# Revit family: Andy v5.5
name_source: partatom
category: Entourage
units: mm (PartAtom-declared; Revit-internal decimal feet)

## family parameters
Always vertical = Yes
Cut with Voids When Loaded = No
Render Appearance Source = Family Geometry
Room Calculation Point = No
Shared = No
Work Plane-Based = No

## types (10) — shared parameters
Description = Multi-positionable human with multiple body profiles for use in 3D views and rendering
Hip Azimuth = 0.00°
Hip Azimuth Label = 1.00°
Inspecting = No
Kinship = www.kinship.io
Kneeling = No
Left Ankle Azimuth Label = 1.00°
Left Thigh Azimuth Label = 1.00°
Length 1 = 0.167 '
Manufacturer = Kinship
Min Angle = 1.00°
Model = Andy v5.5
Neck Rotation = 90.00°
Neck Rotation Label = 90.00°
Praying = No
Right Ankle Azimuth Label = 1.00°
Right Ankle Pitch Label = 181.00°
Right Hand Azimuth = 90.00°
Right Hand Azimuth Label = 90.00°
Right Thigh Azimuth Label = 1.00°
Running = No
Sitting = No
Standing = Yes
Torso Pitch = 91.00°
URL = www.kinship.io
Walking = No
zero-valued in all types: Height

## per-type parameters (varying)
- Walking 1 - Child 2: Ankle Radius=0.071 '; Ankle Radius 2=0.071 '; Calf Length=0.882 '; Chest Depth=0.682 '; Chest Half Depth=0.341 '; Chest Half Depth Back Label=0.288 '; Chest Half Depth Front Label=0.395 '; Chest Half Width=0.427 '; Chest Offset=0.054 '; Chest Width=0.853 '; Chest to Shoulder Height=0.252 '; Child=Yes; Chin to Eye Height=0.338 '; Elbow Radius=0.064 '; Elbow Radius 2=0.064 '; Female=Yes; Foot Height=0.212 '; Foot Length=0.547 '; Foot Width Radius=0.114 '; Fore Arm Length=0.679 '; Hand Depth=0.079 '; Hand Half Depth=0.039 '; Hand Half Length=0.194 '; Hand Half Width=0.102 '; Hand Length=0.388 '; Hand Width=0.204 '; Head Azimuth=0.00°; Head Azimuth Label=1.00°; Head Back Depth=0.199 '; Head Depth=0.569 '; Head Front Depth=0.37 '; Head Half Height=0.355 '; Head Half Width=0.22 '; Head Height=0.711 '; Head Pitch=90.00°; Head Width=0.439 '; Heel Radius=0.071 '; Hip Depth=0.463 '; Hip Half Depth=0.231 '; Hip Half Width=0.38 '; Hip Height=2.187 '; Hip Width=0.759 '; Hip to Waist Height=0.355 '; Knee Radius=0.114 '; Knee Radius 2=0.114 '; Left Ankle Azimuth=0.00°; Left Ankle Pitch=184.00°; Left Ankle Pitch Label=184.00°; Left Arm Azimuth=-20.00°; Left Arm Azimuth Label=-20.00°; Left Arm Pitch=-60.00°; Left Arm Pitch Label=-60.00°; Left Elbow Azimuth=230.00°; Left Elbow Azimuth Label=230.00°; Left Hand Azimuth=90.00°; Left Hand Azimuth Label=90.00°; Left Hand Pitch=40.00°; Left Hand Pitch Label=40.00°; Left Hand Rotation=170.00°; Left Hand Rotation Label=170.00°; Left Knee Pitch=173.00°; Left Knee Pitch Label=173.00°; Left Thigh Azimuth=1.00°; Left Thigh Pitch=105.00°; Left Thigh Pitch Label=105.00°; Length 10=-0.039 '; Length 11=0.026 '; Length 2=0.362 '; Length 3=-0.212 '; Length 4=-0.212 '; Length 5=-0.711 '; Length 6=-0.252 '; Length 7=0.199 '; Length 8=0.15 '; Length 9=0.136 '; Male 1=Yes; Male 2=No; Neck Height=0.213 '; Neck Pitch=90.00°; Neck Pitch Label=90.00°; Neck Radius=0.111 '; Right Ankle Azimuth=0.00°; Right Ankle Pitch=181.00°; Right Arm Azimuth=10.00°; Right Arm Azimuth Label=10.00°; Right Arm Pitch=105.00°; Right Arm Pitch Label=105.00°; Right Elbow Azimuth=135.00°; Right Elbow Azimuth Label=135.00°; Right Hand Pitch=10.00°; Right Hand Pitch Label=10.00°; Right Hand Rotation=10.00°; Right Hand Rotation Label=10.00°; Right Knee Pitch=123.00°; Right Knee Pitch Label=123.00°; Right Thigh Azimuth=1.00°; Right Thigh Pitch=94.00°; Right Thigh Pitch Label=94.00°; Shoulder Depth=0.422 '; Shoulder Half Depth=0.211 '; Shoulder Half Width 1=0.414 '; Shoulder Half Width 2=0.517 '; Shoulder Radius=0.103 '; Shoulder Radius 2=0.103 '; Shoulder Width=1.034 '; Shoulder to Neck Base Height=0.245 '; Thigh Length=1.094 '; Thigh Radius=0.185 '; Thigh Radius 2=0.185 '; Torso Azimuth=92.00°; Total Height=4.265 '; Type Comments=Walking position 4.25 ft child.; Upper Arm Length=0.782 '; Upper Arm Radius=0.126 '; Waist Depth=0.509 '; Waist Half Depth=0.255 '; Waist Half Depth Back Label=0.255 '; Waist Half Depth Front Label=0.255 '; Waist Half Width=0.345 '; Waist Offset=0 '; Waist Width=0.69 '; Waist to Chest Height=0.711 '; Wrist Radius=0.039 '; Wrist Radius 2=0.039 '; a=1.056 '; b=1.083 '; c=0.091 '
- Walking 2 - Female: Ankle Radius=0.088 '; Ankle Radius 2=0.088 '; Calf Length=1.102 '; Chest Depth=0.853 '; Chest Half Depth=0.427 '; Chest Half Depth Back Label=0.3 '; Chest Half Depth Front Label=0.553 '; Chest Half Width=0.533 '; Chest Offset=0.126 '; Chest Width=1.066 '; Chest to Shoulder Height=0.316 '; Child=No; Chin to Eye Height=0.344 '; Elbow Radius=0.08 '; Elbow Radius 2=0.08 '; Female=Yes; Foot Height=0.265 '; Foot Length=0.684 '; Foot Width Radius=0.143 '; Fore Arm Length=0.848 '; Hand Depth=0.091 '; Hand Half Depth=0.045 '; Hand Half Length=0.242 '; Hand Half Width=0.128 '; Hand Length=0.485 '; Hand Width=0.255 '; Head Azimuth=0.00°; Head Azimuth Label=1.00°; Head Back Depth=0.193 '; Head Depth=0.55 '; Head Front Depth=0.358 '; Head Half Height=0.344 '; Head Half Width=0.213 '; Head Height=0.688 '; Head Pitch=90.00°; Head Width=0.425 '; Heel Radius=0.088 '; Hip Depth=0.579 '; Hip Half Depth=0.289 '; Hip Half Width=0.474 '; Hip Height=2.734 '; Hip Width=0.949 '; Hip to Waist Height=0.344 '; Knee Radius=0.143 '; Knee Radius 2=0.143 '; Left Ankle Azimuth=0.00°; Left Ankle Pitch=184.00°; Left Ankle Pitch Label=184.00°; Left Arm Azimuth=10.00°; Left Arm Azimuth Label=10.00°; Left Arm Pitch=-60.00°; Left Arm Pitch Label=-60.00°; Left Elbow Azimuth=230.00°; Left Elbow Azimuth Label=230.00°; Left Hand Azimuth=90.00°; Left Hand Azimuth Label=90.00°; Left Hand Pitch=5.00°; Left Hand Pitch Label=5.00°; Left Hand Rotation=-90.00°; Left Hand Rotation Label=-90.00°; Left Knee Pitch=173.00°; Left Knee Pitch Label=173.00°; Left Thigh Azimuth=1.00°; Left Thigh Pitch=105.00°; Left Thigh Pitch Label=105.00°; Length 10=-0.045 '; Length 11=0.03 '; Length 2=0.452 '; Length 3=-0.265 '; Length 4=-0.265 '; Length 5=-0.989 '; Length 6=-0.316 '; Length 7=0.193 '; Length 8=0.145 '; Length 9=0.131 '; Male 1=Yes; Male 2=No; Neck Height=0.407 '; Neck Pitch=90.00°; Neck Pitch Label=90.00°; Neck Radius=0.139 '; Right Ankle Azimuth=0.00°; Right Ankle Pitch=181.00°; Right Arm Azimuth=10.00°; Right Arm Azimuth Label=10.00°; Right Arm Pitch=105.00°; Right Arm Pitch Label=105.00°; Right Elbow Azimuth=135.00°; Right Elbow Azimuth Label=135.00°; Right Hand Pitch=10.00°; Right Hand Pitch Label=10.00°; Right Hand Rotation=10.00°; Right Hand Rotation Label=10.00°; Right Knee Pitch=123.00°; Right Knee Pitch Label=123.00°; Right Thigh Azimuth=1.00°; Right Thigh Pitch=94.00°; Right Thigh Pitch Label=94.00°; Shoulder Depth=0.527 '; Shoulder Half Depth=0.264 '; Shoulder Half Width 1=0.517 '; Shoulder Half Width 2=0.646 '; Shoulder Radius=0.129 '; Shoulder Radius 2=0.129 '; Shoulder Width=1.292 '; Shoulder to Neck Base Height=0.266 '; Thigh Length=1.367 '; Thigh Radius=0.231 '; Thigh Radius 2=0.231 '; Torso Azimuth=92.00°; Total Height=5.331 '; Type Comments=Walking position 5.3 ft female.; Upper Arm Length=0.977 '; Upper Arm Radius=0.157 '; Waist Depth=0.445 '; Waist Half Depth=0.223 '; Waist Half Depth Back Label=0.223 '; Waist Half Depth Front Label=0.223 '; Waist Half Width=0.365 '; Waist Offset=0 '; Waist Width=0.73 '; Waist to Chest Height=0.989 '; Wrist Radius=0.045 '; Wrist Radius 2=0.045 '; a=1.32 '; b=1.354 '; c=0.114 '
- Walking 4 - Male 2: Ankle Radius=0.125 '; Ankle Radius 2=0.125 '; Calf Length=1.191 '; Chest Depth=0.738 '; Chest Half Depth=0.369 '; Chest Half Depth Back Label=0.369 '; Chest Half Depth Front Label=0.369 '; Chest Half Width=0.591 '; Chest Offset=0 '; Chest Width=1.181 '; Chest to Shoulder Height=0.309 '; Child=No; Chin to Eye Height=0.394 '; Elbow Radius=0.113 '; Elbow Radius 2=0.113 '; Female=No; Foot Height=0.286 '; Foot Length=0.844 '; Foot Width Radius=0.203 '; Fore Arm Length=0.94 '; Hand Depth=0.161 '; Hand Half Depth=0.081 '; Hand Half Length=0.268 '; Hand Half Width=0.166 '; Hand Length=0.537 '; Hand Width=0.332 '; Head Azimuth=0.00°; Head Azimuth Label=1.00°; Head Back Depth=0.22 '; Head Depth=0.63 '; Head Front Depth=0.409 '; Head Half Height=0.394 '; Head Half Width=0.262 '; Head Height=0.787 '; Head Pitch=90.00°; Head Width=0.525 '; Heel Radius=0.125 '; Hip Depth=0.821 '; Hip Half Depth=0.41 '; Hip Half Width=0.607 '; Hip Height=2.953 '; Hip Width=1.215 '; Hip to Waist Height=0.394 '; Knee Radius=0.203 '; Knee Radius 2=0.203 '; Left Ankle Azimuth=0.00°; Left Ankle Pitch=184.00°; Left Ankle Pitch Label=184.00°; Left Arm Azimuth=10.00°; Left Arm Azimuth Label=10.00°; Left Arm Pitch=-105.00°; Left Arm Pitch Label=-105.00°; Left Elbow Azimuth=182.00°; Left Elbow Azimuth Label=182.00°; Left Hand Azimuth=90.00°; Left Hand Azimuth Label=90.00°; Left Hand Pitch=5.00°; Left Hand Pitch Label=5.00°; Left Hand Rotation=-90.00°; Left Hand Rotation Label=-90.00°; Left Knee Pitch=173.00°; Left Knee Pitch Label=173.00°; Left Thigh Azimuth=1.00°; Left Thigh Pitch=105.00°; Left Thigh Pitch Label=105.00°; Length 10=-0.081 '; Length 11=0.054 '; Length 2=0.515 '; Length 3=-0.286 '; Length 4=-0.286 '; Length 5=-1.083 '; Length 6=-0.309 '; Length 7=0.22 '; Length 8=0.147 '; Length 9=0.131 '; Male 1=No; Male 2=Yes; Neck Height=0.433 '; Neck Pitch=90.00°; Neck Pitch Label=90.00°; Neck Radius=0.182 '; Right Ankle Azimuth=0.00°; Right Ankle Pitch=181.00°; Right Arm Azimuth=10.00°; Right Arm Azimuth Label=10.00°; Right Arm Pitch=90.00°; Right Arm Pitch Label=90.00°; Right Elbow Azimuth=145.00°; Right Elbow Azimuth Label=145.00°; Right Hand Pitch=10.00°; Right Hand Pitch Label=10.00°; Right Hand Rotation=10.00°; Right Hand Rotation Label=10.00°; Right Knee Pitch=123.00°; Right Knee Pitch Label=123.00°; Right Thigh Azimuth=1.00°; Right Thigh Pitch=94.00°; Right Thigh Pitch Label=94.00°; Shoulder Depth=0.591 '; Shoulder Half Depth=0.295 '; Shoulder Half Width 1=0.556 '; Shoulder Half Width 2=0.738 '; Shoulder Radius=0.183 '; Shoulder Radius 2=0.183 '; Shoulder Width=1.476 '; Shoulder to Neck Base Height=0.34 '; Thigh Length=1.476 '; Thigh Radius=0.328 '; Thigh Radius 2=0.328 '; Torso Azimuth=92.00°; Total Height=5.906 '; Type Comments=Walking position 6 ft male 2.; Upper Arm Length=1.083 '; Upper Arm Radius=0.223 '; Waist Depth=1.067 '; Waist Half Depth=0.534 '; Waist Half Depth Back Label=0.399 '; Waist Half Depth Front Label=0.669 '; Waist Half Width=0.607 '; Waist Offset=0.135 '; Waist Width=1.215 '; Waist to Chest Height=1.083 '; Wrist Radius=0.081 '; Wrist Radius 2=0.081 '; a=1.426 '; b=1.462 '; c=0.137 '
- Walking 3 - Male 1: Ankle Radius=0.109 '; Ankle Radius 2=0.109 '; Calf Length=1.124 '; Chest Depth=0.744 '; Chest Half Depth=0.372 '; Chest Half Depth Back Label=0.327 '; Chest Half Depth Front Label=0.416 '; Chest Half Width=0.558 '; Chest Offset=0.045 '; Chest Width=1.115 '; Chest to Shoulder Height=0.306 '; Child=No; Chin to Eye Height=0.372 '; Elbow Radius=0.098 '; Elbow Radius 2=0.098 '; Female=No; Foot Height=0.27 '; Foot Length=0.797 '; Foot Width Radius=0.177 '; Fore Arm Length=0.887 '; Hand Depth=0.14 '; Hand Half Depth=0.07 '; Hand Half Length=0.254 '; Hand Half Width=0.157 '; Hand Length=0.507 '; Hand Width=0.313 '; Head Azimuth=0.00°; Head Azimuth Label=1.00°; Head Back Depth=0.208 '; Head Depth=0.595 '; Head Front Depth=0.387 '; Head Half Height=0.372 '; Head Half Width=0.248 '; Head Height=0.744 '; Head Pitch=90.00°; Head Width=0.496 '; Heel Radius=0.109 '; Hip Depth=0.715 '; Hip Half Depth=0.358 '; Hip Half Width=0.558 '; Hip Height=2.789 '; Hip Width=1.115 '; Hip to Waist Height=0.372 '; Knee Radius=0.177 '; Knee Radius 2=0.177 '; Left Ankle Azimuth=0.00°; Left Ankle Pitch=184.00°; Left Ankle Pitch Label=184.00°; Left Arm Azimuth=182.00°; Left Arm Azimuth Label=182.00°; Left Arm Pitch=-90.00°; Left Arm Pitch Label=-90.00°; Left Elbow Azimuth=145.00°; Left Elbow Azimuth Label=145.00°; Left Hand Azimuth=90.00°; Left Hand Azimuth Label=90.00°; Left Hand Pitch=5.00°; Left Hand Pitch Label=5.00°; Left Hand Rotation=60.00°; Left Hand Rotation Label=60.00°; Left Knee Pitch=173.00°; Left Knee Pitch Label=173.00°; Left Thigh Azimuth=1.00°; Left Thigh Pitch=105.00°; Left Thigh Pitch Label=105.00°; Length 10=-0.07 '; Length 11=0.047 '; Length 2=0.511 '; Length 3=-0.27 '; Length 4=-0.27 '; Length 5=-1.023 '; Length 6=-0.306 '; Length 7=0.208 '; Length 8=0.139 '; Length 9=0.124 '; Male 1=Yes; Male 2=No; Neck Height=0.409 '; Neck Pitch=90.00°; Neck Pitch Label=90.00°; Neck Radius=0.142 '; Right Ankle Azimuth=0.00°; Right Ankle Pitch=181.00°; Right Arm Azimuth=10.00°; Right Arm Azimuth Label=10.00°; Right Arm Pitch=105.00°; Right Arm Pitch Label=105.00°; Right Elbow Azimuth=160.00°; Right Elbow Azimuth Label=160.00°; Right Hand Pitch=10.00°; Right Hand Pitch Label=10.00°; Right Hand Rotation=90.00°; Right Hand Rotation Label=90.00°; Right Knee Pitch=123.00°; Right Knee Pitch Label=123.00°; Right Thigh Azimuth=1.00°; Right Thigh Pitch=94.00°; Right Thigh Pitch Label=94.00°; Shoulder Depth=0.46 '; Shoulder Half Depth=0.23 '; Shoulder Half Width 1=0.538 '; Shoulder Half Width 2=0.697 '; Shoulder Radius=0.159 '; Shoulder Radius 2=0.159 '; Shoulder Width=1.394 '; Shoulder to Neck Base Height=0.308 '; Thigh Length=1.394 '; Thigh Radius=0.286 '; Thigh Radius 2=0.286 '; Torso Azimuth=92.00°; Total Height=5.577 '; Type Comments=Walking position 5.5 ft male 1.; Upper Arm Length=1.023 '; Upper Arm Radius=0.194 '; Waist Depth=0.65 '; Waist Half Depth=0.325 '; Waist Half Depth Back Label=0.3 '; Waist Half Depth Front Label=0.35 '; Waist Half Width=0.507 '; Waist Offset=0.025 '; Waist Width=1.014 '; Waist to Chest Height=1.023 '; Wrist Radius=0.07 '; Wrist Radius 2=0.07 '; a=1.347 '; b=1.381 '; c=0.131 '
- Standing 2 - Child 2: Ankle Radius=0.09 '; Ankle Radius 2=0.09 '; Calf Length=0.959 '; Chest Depth=0.634 '; Chest Half Depth=0.317 '; Chest Half Depth Back Label=0.309 '; Chest Half Depth Front Label=0.326 '; Chest Half Width=0.476 '; Chest Offset=0.008 '; Chest Width=0.951 '; Chest to Shoulder Height=0.265 '; Child=Yes; Chin to Eye Height=0.378 '; Elbow Radius=0.081 '; Elbow Radius 2=0.081 '; Female=No; Foot Height=0.23 '; Foot Length=0.68 '; Foot Width Radius=0.146 '; Fore Arm Length=0.757 '; Hand Depth=0.1 '; Hand Half Depth=0.05 '; Hand Half Length=0.216 '; Hand Half Width=0.134 '; Hand Length=0.432 '; Hand Width=0.267 '; Head Azimuth=30.00°; Head Azimuth Label=30.00°; Head Back Depth=0.222 '; Head Depth=0.634 '; Head Front Depth=0.412 '; Head Half Height=0.396 '; Head Half Width=0.264 '; Head Height=0.793 '; Head Pitch=100.00°; Head Width=0.529 '; Heel Radius=0.09 '; Hip Depth=0.59 '; Hip Half Depth=0.295 '; Hip Half Width=0.46 '; Hip Height=2.379 '; Hip Width=0.921 '; Hip to Waist Height=0.396 '; Knee Radius=0.146 '; Knee Radius 2=0.146 '; Left Ankle Azimuth=1.00°; Left Ankle Pitch=180.10°; Left Ankle Pitch Label=180.10°; Left Arm Azimuth=170.00°; Left Arm Azimuth Label=170.00°; Left Arm Pitch=-70.00°; Left Arm Pitch Label=-70.00°; Left Elbow Azimuth=130.00°; Left Elbow Azimuth Label=130.00°; Left Hand Azimuth=90.00°; Left Hand Azimuth Label=90.00°; Left Hand Pitch=1.00°; Left Hand Pitch Label=1.00°; Left Hand Rotation=100.00°; Left Hand Rotation Label=100.00°; Left Knee Pitch=180.00°; Left Knee Pitch Label=180.00°; Left Thigh Azimuth=0.00°; Left Thigh Pitch=90.00°; Left Thigh Pitch Label=90.00°; Length 10=-0.05 '; Length 11=0.033 '; Length 2=0.444 '; Length 3=-0.23 '; Length 4=-0.23 '; Length 5=-0.793 '; Length 6=-0.265 '; Length 7=0.222 '; Length 8=0.148 '; Length 9=0.132 '; Male 1=Yes; Male 2=No; Neck Height=0.238 '; Neck Pitch=80.00°; Neck Pitch Label=80.00°; Neck Radius=0.121 '; Right Ankle Azimuth=1.00°; Right Ankle Pitch=180.00°; Right Arm Azimuth=30.00°; Right Arm Azimuth Label=30.00°; Right Arm Pitch=73.00°; Right Arm Pitch Label=73.00°; Right Elbow Azimuth=138.00°; Right Elbow Azimuth Label=138.00°; Right Hand Pitch=0.00°; Right Hand Pitch Label=1.00°; Right Hand Rotation=-2.00°; Right Hand Rotation Label=-2.00°; Right Knee Pitch=180.00°; Right Knee Pitch Label=181.00°; Right Thigh Azimuth=0.00°; Right Thigh Pitch=90.00°; Right Thigh Pitch Label=90.00°; Shoulder Depth=0.392 '; Shoulder Half Depth=0.196 '; Shoulder Half Width 1=0.463 '; Shoulder Half Width 2=0.595 '; Shoulder Radius=0.131 '; Shoulder Radius 2=0.131 '; Shoulder Width=1.189 '; Shoulder to Neck Base Height=0.29 '; Thigh Length=1.189 '; Thigh Radius=0.236 '; Thigh Radius 2=0.236 '; Torso Azimuth=90.00°; Total Height=4.757 '; Type Comments=Standing position 4.75 ft child 2.; Upper Arm Length=0.872 '; Upper Arm Radius=0.16 '; Waist Depth=0.649 '; Waist Half Depth=0.325 '; Waist Half Depth Back Label=0.304 '; Waist Half Depth Front Label=0.345 '; Waist Half Width=0.418 '; Waist Offset=0.021 '; Waist Width=0.837 '; Waist to Chest Height=0.793 '; Wrist Radius=0.05 '; Wrist Radius 2=0.05 '; a=1.189 '; b=1.189 '; c=0.001 '
- Standing 4 - Male 2 - Holding Hand: Ankle Radius=0.111 '; Ankle Radius 2=0.111 '; Calf Length=1.058 '; Chest Depth=0.656 '; Chest Half Depth=0.328 '; Chest Half Depth Back Label=0.328 '; Chest Half Depth Front Label=0.328 '; Chest Half Width=0.525 '; Chest Offset=0 '; Chest Width=1.05 '; Chest to Shoulder Height=0.275 '; Child=No; Chin to Eye Height=0.35 '; Elbow Radius=0.1 '; Elbow Radius 2=0.1 '; Female=No; Foot Height=0.254 '; Foot Length=0.75 '; Foot Width Radius=0.18 '; Fore Arm Length=0.835 '; Hand Depth=0.143 '; Hand Half Depth=0.072 '; Hand Half Length=0.239 '; Hand Half Width=0.147 '; Hand Length=0.477 '; Hand Width=0.295 '; Head Azimuth=-30.00°; Head Azimuth Label=-30.00°; Head Back Depth=0.196 '; Head Depth=0.56 '; Head Front Depth=0.364 '; Head Half Height=0.35 '; Head Half Width=0.233 '; Head Height=0.7 '; Head Pitch=80.00°; Head Width=0.467 '; Heel Radius=0.111 '; Hip Depth=0.73 '; Hip Half Depth=0.365 '; Hip Half Width=0.54 '; Hip Height=2.625 '; Hip Width=1.08 '; Hip to Waist Height=0.35 '; Knee Radius=0.18 '; Knee Radius 2=0.18 '; Left Ankle Azimuth=1.00°; Left Ankle Pitch=180.10°; Left Ankle Pitch Label=180.10°; Left Arm Azimuth=160.00°; Left Arm Azimuth Label=160.00°; Left Arm Pitch=-70.00°; Left Arm Pitch Label=-70.00°; Left Elbow Azimuth=108.00°; Left Elbow Azimuth Label=108.00°; Left Hand Azimuth=90.00°; Left Hand Azimuth Label=90.00°; Left Hand Pitch=1.00°; Left Hand Pitch Label=1.00°; Left Hand Rotation=80.00°; Left Hand Rotation Label=80.00°; Left Knee Pitch=180.00°; Left Knee Pitch Label=180.00°; Left Thigh Azimuth=0.00°; Left Thigh Pitch=90.00°; Left Thigh Pitch Label=90.00°; Length 10=-0.072 '; Length 11=0.048 '; Length 2=0.458 '; Length 3=-0.254 '; Length 4=-0.254 '; Length 5=-0.962 '; Length 6=-0.275 '; Length 7=0.196 '; Length 8=0.131 '; Length 9=0.117 '; Male 1=No; Male 2=Yes; Neck Height=0.385 '; Neck Pitch=100.00°; Neck Pitch Label=100.00°; Neck Radius=0.162 '; Right Ankle Azimuth=1.00°; Right Ankle Pitch=180.00°; Right Arm Azimuth=40.00°; Right Arm Azimuth Label=40.00°; Right Arm Pitch=80.00°; Right Arm Pitch Label=80.00°; Right Elbow Azimuth=157.00°; Right Elbow Azimuth Label=157.00°; Right Hand Pitch=30.00°; Right Hand Pitch Label=30.00°; Right Hand Rotation=-20.00°; Right Hand Rotation Label=-20.00°; Right Knee Pitch=180.00°; Right Knee Pitch Label=181.00°; Right Thigh Azimuth=0.00°; Right Thigh Pitch=90.00°; Right Thigh Pitch Label=90.00°; Shoulder Depth=0.525 '; Shoulder Half Depth=0.262 '; Shoulder Half Width 1=0.494 '; Shoulder Half Width 2=0.656 '; Shoulder Radius=0.162 '; Shoulder Radius 2=0.162 '; Shoulder Width=1.312 '; Shoulder to Neck Base Height=0.302 '; Thigh Length=1.312 '; Thigh Radius=0.292 '; Thigh Radius 2=0.292 '; Torso Azimuth=90.00°; Total Height=5.249 '; Type Comments=Standing position 5.25 ft male 2 holding child's hand.; Upper Arm Length=0.962 '; Upper Arm Radius=0.198 '; Waist Depth=0.949 '; Waist Half Depth=0.474 '; Waist Half Depth Back Label=0.354 '; Waist Half Depth Front Label=0.594 '; Waist Half Width=0.54 '; Waist Offset=0.12 '; Waist Width=1.08 '; Waist to Chest Height=0.962 '; Wrist Radius=0.072 '; Wrist Radius 2=0.072 '; a=1.312 '; b=1.312 '; c=0.001 '
- Standing 3 - Male 1 - Talking: Ankle Radius=0.119 '; Ankle Radius 2=0.119 '; Calf Length=1.224 '; Chest Depth=0.809 '; Chest Half Depth=0.405 '; Chest Half Depth Back Label=0.356 '; Chest Half Depth Front Label=0.453 '; Chest Half Width=0.607 '; Chest Offset=0.049 '; Chest Width=1.214 '; Chest to Shoulder Height=0.333 '; Child=No; Chin to Eye Height=0.405 '; Elbow Radius=0.107 '; Elbow Radius 2=0.107 '; Female=No; Foot Height=0.294 '; Foot Length=0.867 '; Foot Width Radius=0.192 '; Fore Arm Length=0.966 '; Hand Depth=0.153 '; Hand Half Depth=0.076 '; Hand Half Length=0.276 '; Hand Half Width=0.171 '; Hand Length=0.552 '; Hand Width=0.341 '; Head Azimuth=40.00°; Head Azimuth Label=40.00°; Head Back Depth=0.227 '; Head Depth=0.647 '; Head Front Depth=0.421 '; Head Half Height=0.405 '; Head Half Width=0.27 '; Head Height=0.809 '; Head Pitch=100.00°; Head Width=0.54 '; Heel Radius=0.119 '; Hip Depth=0.778 '; Hip Half Depth=0.389 '; Hip Half Width=0.607 '; Hip Height=3.035 '; Hip Width=1.214 '; Hip to Waist Height=0.405 '; Knee Radius=0.192 '; Knee Radius 2=0.192 '; Left Ankle Azimuth=1.00°; Left Ankle Pitch=180.10°; Left Ankle Pitch Label=180.10°; Left Arm Azimuth=160.00°; Left Arm Azimuth Label=160.00°; Left Arm Pitch=-70.00°; Left Arm Pitch Label=-70.00°; Left Elbow Azimuth=128.00°; Left Elbow Azimuth Label=128.00°; Left Hand Azimuth=100.00°; Left Hand Azimuth Label=100.00°; Left Hand Pitch=30.00°; Left Hand Pitch Label=30.00°; Left Hand Rotation=0.00°; Left Hand Rotation Label=1.00°; Left Knee Pitch=180.00°; Left Knee Pitch Label=180.00°; Left Thigh Azimuth=0.00°; Left Thigh Pitch=90.00°; Left Thigh Pitch Label=90.00°; Length 10=-0.076 '; Length 11=0.051 '; Length 2=0.556 '; Length 3=-0.294 '; Length 4=-0.294 '; Length 5=-1.113 '; Length 6=-0.333 '; Length 7=0.227 '; Length 8=0.151 '; Length 9=0.135 '; Male 1=Yes; Male 2=No; Neck Height=0.445 '; Neck Pitch=95.00°; Neck Pitch Label=95.00°; Neck Radius=0.155 '; Right Ankle Azimuth=1.00°; Right Ankle Pitch=180.00°; Right Arm Azimuth=10.00°; Right Arm Azimuth Label=10.00°; Right Arm Pitch=50.00°; Right Arm Pitch Label=50.00°; Right Elbow Azimuth=50.00°; Right Elbow Azimuth Label=50.00°; Right Hand Pitch=30.00°; Right Hand Pitch Label=30.00°; Right Hand Rotation=80.00°; Right Hand Rotation Label=80.00°; Right Knee Pitch=180.00°; Right Knee Pitch Label=181.00°; Right Thigh Azimuth=0.00°; Right Thigh Pitch=90.00°; Right Thigh Pitch Label=90.00°; Shoulder Depth=0.5 '; Shoulder Half Depth=0.25 '; Shoulder Half Width 1=0.586 '; Shoulder Half Width 2=0.759 '; Shoulder Radius=0.173 '; Shoulder Radius 2=0.173 '; Shoulder Width=1.517 '; Shoulder to Neck Base Height=0.335 '; Thigh Length=1.517 '; Thigh Radius=0.311 '; Thigh Radius 2=0.311 '; Torso Azimuth=90.00°; Total Height=6.07 '; Type Comments=Standing position 6ft male 1.; Upper Arm Length=1.113 '; Upper Arm Radius=0.212 '; Waist Depth=0.707 '; Waist Half Depth=0.354 '; Waist Half Depth Back Label=0.326 '; Waist Half Depth Front Label=0.381 '; Waist Half Width=0.552 '; Waist Offset=0.028 '; Waist Width=1.104 '; Waist to Chest Height=1.113 '; Wrist Radius=0.076 '; Wrist Radius 2=0.076 '; a=1.517 '; b=1.517 '; c=0.001 '
- Standing 5 - Male 2 - Talking: Ankle Radius=0.125 '; Ankle Radius 2=0.125 '; Calf Length=1.191 '; Chest Depth=0.738 '; Chest Half Depth=0.369 '; Chest Half Depth Back Label=0.369 '; Chest Half Depth Front Label=0.369 '; Chest Half Width=0.591 '; Chest Offset=0 '; Chest Width=1.181 '; Chest to Shoulder Height=0.309 '; Child=No; Chin to Eye Height=0.394 '; Elbow Radius=0.113 '; Elbow Radius 2=0.113 '; Female=No; Foot Height=0.286 '; Foot Length=0.844 '; Foot Width Radius=0.203 '; Fore Arm Length=0.94 '; Hand Depth=0.161 '; Hand Half Depth=0.081 '; Hand Half Length=0.268 '; Hand Half Width=0.166 '; Hand Length=0.537 '; Hand Width=0.332 '; Head Azimuth=10.00°; Head Azimuth Label=10.00°; Head Back Depth=0.22 '; Head Depth=0.63 '; Head Front Depth=0.409 '; Head Half Height=0.394 '; Head Half Width=0.262 '; Head Height=0.787 '; Head Pitch=100.00°; Head Width=0.525 '; Heel Radius=0.125 '; Hip Depth=0.821 '; Hip Half Depth=0.41 '; Hip Half Width=0.607 '; Hip Height=2.953 '; Hip Width=1.215 '; Hip to Waist Height=0.394 '; Knee Radius=0.203 '; Knee Radius 2=0.203 '; Left Ankle Azimuth=1.00°; Left Ankle Pitch=180.10°; Left Ankle Pitch Label=180.10°; Left Arm Azimuth=160.00°; Left Arm Azimuth Label=160.00°; Left Arm Pitch=-70.00°; Left Arm Pitch Label=-70.00°; Left Elbow Azimuth=115.00°; Left Elbow Azimuth Label=115.00°; Left Hand Azimuth=90.00°; Left Hand Azimuth Label=90.00°; Left Hand Pitch=2.00°; Left Hand Pitch Label=2.00°; Left Hand Rotation=120.00°; Left Hand Rotation Label=120.00°; Left Knee Pitch=180.00°; Left Knee Pitch Label=180.00°; Left Thigh Azimuth=0.00°; Left Thigh Pitch=90.00°; Left Thigh Pitch Label=90.00°; Length 10=-0.081 '; Length 11=0.054 '; Length 2=0.515 '; Length 3=-0.286 '; Length 4=-0.286 '; Length 5=-1.083 '; Length 6=-0.309 '; Length 7=0.22 '; Length 8=0.147 '; Length 9=0.131 '; Male 1=No; Male 2=Yes; Neck Height=0.433 '; Neck Pitch=85.00°; Neck Pitch Label=85.00°; Neck Radius=0.182 '; Right Ankle Azimuth=1.00°; Right Ankle Pitch=180.00°; Right Arm Azimuth=70.00°; Right Arm Azimuth Label=70.00°; Right Arm Pitch=80.00°; Right Arm Pitch Label=80.00°; Right Elbow Azimuth=98.00°; Right Elbow Azimuth Label=98.00°; Right Hand Pitch=27.00°; Right Hand Pitch Label=27.00°; Right Hand Rotation=10.00°; Right Hand Rotation Label=10.00°; Right Knee Pitch=180.00°; Right Knee Pitch Label=181.00°; Right Thigh Azimuth=0.00°; Right Thigh Pitch=90.00°; Right Thigh Pitch Label=90.00°; Shoulder Depth=0.591 '; Shoulder Half Depth=0.295 '; Shoulder Half Width 1=0.556 '; Shoulder Half Width 2=0.738 '; Shoulder Radius=0.183 '; Shoulder Radius 2=0.183 '; Shoulder Width=1.476 '; Shoulder to Neck Base Height=0.34 '; Thigh Length=1.476 '; Thigh Radius=0.328 '; Thigh Radius 2=0.328 '; Torso Azimuth=90.00°; Total Height=5.906 '; Type Comments=Standing position 6 ft male 2 talking.; Upper Arm Length=1.083 '; Upper Arm Radius=0.223 '; Waist Depth=1.067 '; Waist Half Depth=0.534 '; Waist Half Depth Back Label=0.399 '; Waist Half Depth Front Label=0.669 '; Waist Half Width=0.607 '; Waist Offset=0.135 '; Waist Width=1.215 '; Waist to Chest Height=1.083 '; Wrist Radius=0.081 '; Wrist Radius 2=0.081 '; a=1.476 '; b=1.476 '; c=0.001 '
- Standing 1 - Child 1 - Holding Hand: Ankle Radius=0.062 '; Ankle Radius 2=0.062 '; Calf Length=0.661 '; Chest Depth=0.437 '; Chest Half Depth=0.219 '; Chest Half Depth Back Label=0.213 '; Chest Half Depth Front Label=0.224 '; Chest Half Width=0.328 '; Chest Offset=0.006 '; Chest Width=0.656 '; Chest to Shoulder Height=0.183 '; Child=Yes; Chin to Eye Height=0.26 '; Elbow Radius=0.056 '; Elbow Radius 2=0.056 '; Female=No; Foot Height=0.159 '; Foot Length=0.469 '; Foot Width Radius=0.101 '; Fore Arm Length=0.522 '; Hand Depth=0.069 '; Hand Half Depth=0.035 '; Hand Half Length=0.149 '; Hand Half Width=0.092 '; Hand Length=0.298 '; Hand Width=0.184 '; Head Azimuth=30.00°; Head Azimuth Label=30.00°; Head Back Depth=0.153 '; Head Depth=0.437 '; Head Front Depth=0.284 '; Head Half Height=0.273 '; Head Half Width=0.182 '; Head Height=0.547 '; Head Pitch=100.00°; Head Width=0.365 '; Heel Radius=0.062 '; Hip Depth=0.407 '; Hip Half Depth=0.203 '; Hip Half Width=0.317 '; Hip Height=1.64 '; Hip Width=0.635 '; Hip to Waist Height=0.273 '; Knee Radius=0.101 '; Knee Radius 2=0.101 '; Left Ankle Azimuth=1.00°; Left Ankle Pitch=180.10°; Left Ankle Pitch Label=180.10°; Left Arm Azimuth=170.00°; Left Arm Azimuth Label=170.00°; Left Arm Pitch=-70.00°; Left Arm Pitch Label=-70.00°; Left Elbow Azimuth=120.00°; Left Elbow Azimuth Label=120.00°; Left Hand Azimuth=90.00°; Left Hand Azimuth Label=90.00°; Left Hand Pitch=-30.00°; Left Hand Pitch Label=-30.00°; Left Hand Rotation=161.00°; Left Hand Rotation Label=161.00°; Left Knee Pitch=180.00°; Left Knee Pitch Label=180.00°; Left Thigh Azimuth=0.00°; Left Thigh Pitch=90.00°; Left Thigh Pitch Label=90.00°; Length 10=-0.035 '; Length 11=0.023 '; Length 2=0.306 '; Length 3=-0.159 '; Length 4=-0.159 '; Length 5=-0.547 '; Length 6=-0.183 '; Length 7=0.153 '; Length 8=0.102 '; Length 9=0.091 '; Male 1=Yes; Male 2=No; Neck Height=0.164 '; Neck Pitch=80.00°; Neck Pitch Label=80.00°; Neck Radius=0.084 '; Right Ankle Azimuth=1.00°; Right Ankle Pitch=180.00°; Right Arm Azimuth=60.00°; Right Arm Azimuth Label=60.00°; Right Arm Pitch=75.00°; Right Arm Pitch Label=75.00°; Right Elbow Azimuth=50.00°; Right Elbow Azimuth Label=50.00°; Right Hand Pitch=-25.00°; Right Hand Pitch Label=-25.00°; Right Hand Rotation=181.00°; Right Hand Rotation Label=181.00°; Right Knee Pitch=180.00°; Right Knee Pitch Label=181.00°; Right Thigh Azimuth=0.00°; Right Thigh Pitch=90.00°; Right Thigh Pitch Label=90.00°; Shoulder Depth=0.27 '; Shoulder Half Depth=0.135 '; Shoulder Half Width 1=0.32 '; Shoulder Half Width 2=0.41 '; Shoulder Radius=0.091 '; Shoulder Radius 2=0.091 '; Shoulder Width=0.82 '; Shoulder to Neck Base Height=0.2 '; Thigh Length=0.82 '; Thigh Radius=0.163 '; Thigh Radius 2=0.163 '; Torso Azimuth=90.00°; Total Height=3.281 '; Type Comments=Standing position 3.3 ft child holding hand.; Upper Arm Length=0.601 '; Upper Arm Radius=0.111 '; Waist Depth=0.448 '; Waist Half Depth=0.224 '; Waist Half Depth Back Label=0.209 '; Waist Half Depth Front Label=0.238 '; Waist Half Width=0.289 '; Waist Offset=0.014 '; Waist Width=0.577 '; Waist to Chest Height=0.547 '; Wrist Radius=0.035 '; Wrist Radius 2=0.035 '; a=0.82 '; b=0.82 '; c=0.001 '
- Standing 3 - Female - Holding Hand: Ankle Radius=0.087 '; Ankle Radius 2=0.087 '; Calf Length=1.085 '; Chest Depth=0.84 '; Chest Half Depth=0.42 '; Chest Half Depth Back Label=0.296 '; Chest Half Depth Front Label=0.544 '; Chest Half Width=0.525 '; Chest Offset=0.124 '; Chest Width=1.05 '; Chest to Shoulder Height=0.311 '; Child=No; Chin to Eye Height=0.339 '; Elbow Radius=0.078 '; Elbow Radius 2=0.078 '; Female=Yes; Foot Height=0.261 '; Foot Length=0.673 '; Foot Width Radius=0.141 '; Fore Arm Length=0.835 '; Hand Depth=0.09 '; Hand Half Depth=0.045 '; Hand Half Length=0.239 '; Hand Half Width=0.126 '; Hand Length=0.477 '; Hand Width=0.251 '; Head Azimuth=-30.00°; Head Azimuth Label=-30.00°; Head Back Depth=0.19 '; Head Depth=0.542 '; Head Front Depth=0.352 '; Head Half Height=0.339 '; Head Half Width=0.209 '; Head Height=0.677 '; Head Pitch=80.00°; Head Width=0.419 '; Heel Radius=0.087 '; Hip Depth=0.57 '; Hip Half Depth=0.285 '; Hip Half Width=0.467 '; Hip Height=2.692 '; Hip Width=0.934 '; Hip to Waist Height=0.339 '; Knee Radius=0.141 '; Knee Radius 2=0.141 '; Left Ankle Azimuth=1.00°; Left Ankle Pitch=180.10°; Left Ankle Pitch Label=180.10°; Left Arm Azimuth=160.00°; Left Arm Azimuth Label=160.00°; Left Arm Pitch=-70.00°; Left Arm Pitch Label=-70.00°; Left Elbow Azimuth=115.00°; Left Elbow Azimuth Label=115.00°; Left Hand Azimuth=90.00°; Left Hand Azimuth Label=90.00°; Left Hand Pitch=1.00°; Left Hand Pitch Label=1.00°; Left Hand Rotation=90.00°; Left Hand Rotation Label=90.00°; Left Knee Pitch=180.00°; Left Knee Pitch Label=180.00°; Left Thigh Azimuth=0.00°; Left Thigh Pitch=90.00°; Left Thigh Pitch Label=90.00°; Length 10=-0.045 '; Length 11=0.03 '; Length 2=0.445 '; Length 3=-0.261 '; Length 4=-0.261 '; Length 5=-0.974 '; Length 6=-0.311 '; Length 7=0.19 '; Length 8=0.143 '; Length 9=0.129 '; Male 1=No; Male 2=No; Neck Height=0.401 '; Neck Pitch=100.00°; Neck Pitch Label=100.00°; Neck Radius=0.137 '; Right Ankle Azimuth=1.00°; Right Ankle Pitch=180.00°; Right Arm Azimuth=40.00°; Right Arm Azimuth Label=40.00°; Right Arm Pitch=80.00°; Right Arm Pitch Label=80.00°; Right Elbow Azimuth=157.00°; Right Elbow Azimuth Label=157.00°; Right Hand Pitch=30.00°; Right Hand Pitch Label=30.00°; Right Hand Rotation=-20.00°; Right Hand Rotation Label=-20.00°; Right Knee Pitch=180.00°; Right Knee Pitch Label=181.00°; Right Thigh Azimuth=0.00°; Right Thigh Pitch=90.00°; Right Thigh Pitch Label=90.00°; Shoulder Depth=0.519 '; Shoulder Half Depth=0.26 '; Shoulder Half Width 1=0.51 '; Shoulder Half Width 2=0.636 '; Shoulder Radius=0.127 '; Shoulder Radius 2=0.127 '; Shoulder Width=1.273 '; Shoulder to Neck Base Height=0.262 '; Thigh Length=1.346 '; Thigh Radius=0.228 '; Thigh Radius 2=0.228 '; Torso Azimuth=90.00°; Total Height=5.249 '; Type Comments=Standing position 5.25 ft female holding child's hand.; Upper Arm Length=0.962 '; Upper Arm Radius=0.155 '; Waist Depth=0.438 '; Waist Half Depth=0.219 '; Waist Half Depth Back Label=0.219 '; Waist Half Depth Front Label=0.219 '; Waist Half Width=0.359 '; Waist Offset=0 '; Waist Width=0.719 '; Waist to Chest Height=0.974 '; Wrist Radius=0.045 '; Wrist Radius 2=0.045 '; a=1.346 '; b=1.346 '; c=0.001 '

## geometry (parser evidence)
native form markers: Sweep x3
no freeform markers — native parametric forms only
